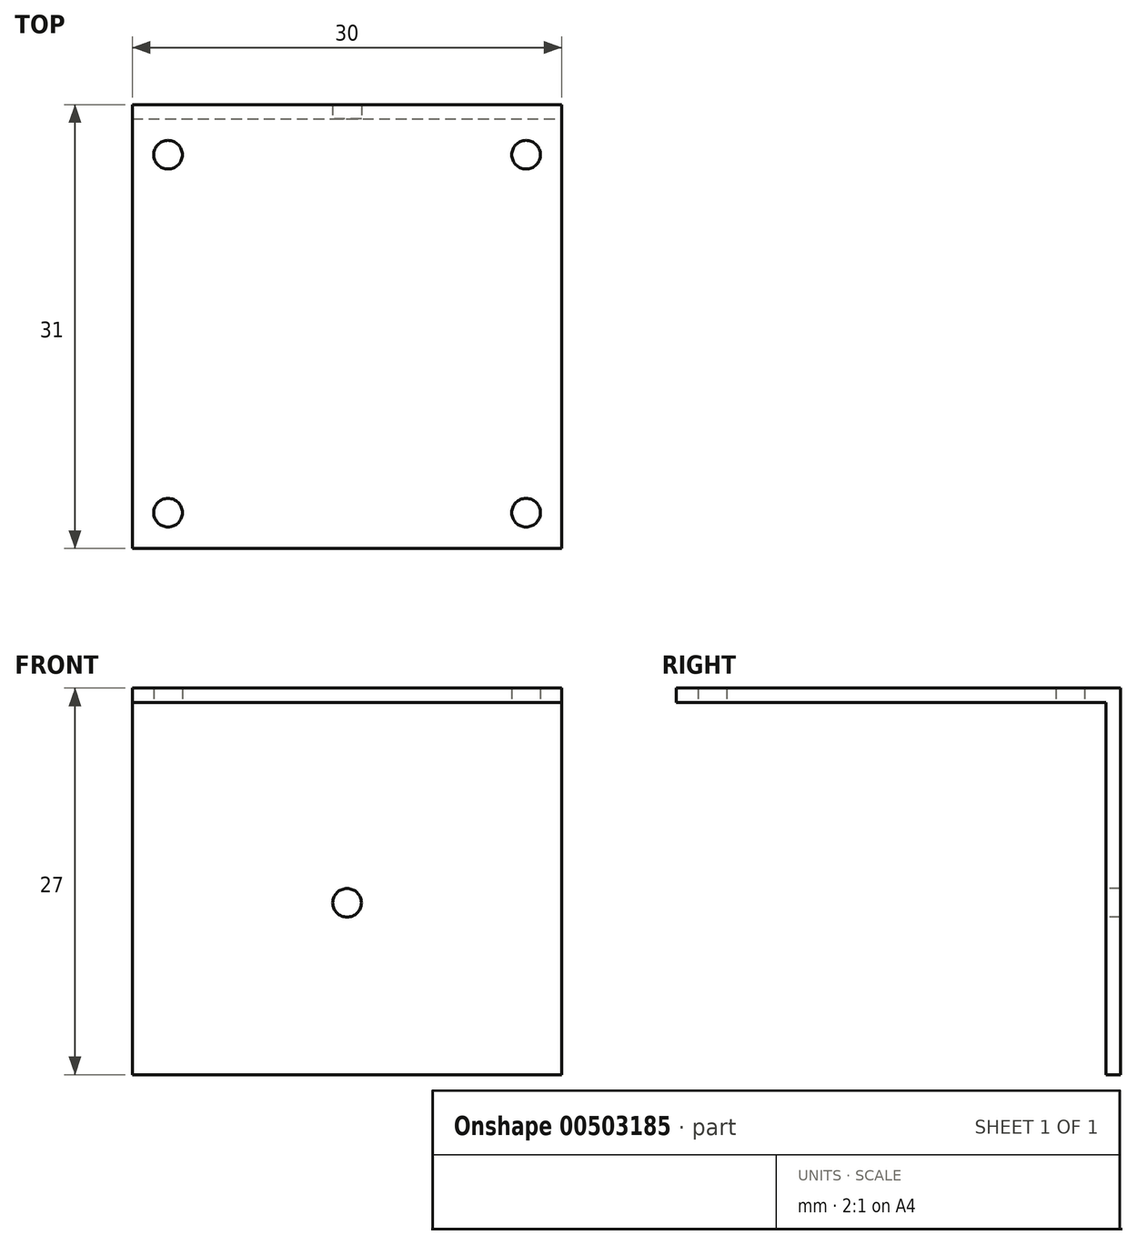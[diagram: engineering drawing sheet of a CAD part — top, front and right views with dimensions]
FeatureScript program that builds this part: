
annotation { "Feature Type Name" : "Feature", "Feature Type Description" : "" }
export const myFeature = defineFeature(function(context is Context, id is Id, definition is map)
    precondition{}
    {
        {
            var Q0;
            Q0=qCreatedBy(makeId("Top.planeOp"),FACE);
            var sketch = newSketch(context, id + "F0", { "sketchPlane" : qUnion([Q0])});
            skLineSegment(sketch, "E0.bottom", {"start": v(-15, 15) * mm, "end": v(15, 15) * mm});
            skLineSegment(sketch, "E0.top", {"start": v(-15, -15) * mm, "end": v(15, -15) * mm});
            skLineSegment(sketch, "E0.left", {"start": v(-15, 15) * mm, "end": v(-15, -15) * mm});
            skLineSegment(sketch, "E0.right", {"start": v(15, 15) * mm, "end": v(15, -15) * mm});
            skCircle(sketch, "E1", {"center": v(-12.5, -12.5) * mm, "radius": 1 * mm});
            skCircle(sketch, "E2.1.0.0", {"center": v(12.5, -12.5) * mm, "radius": 1 * mm});
            skCircle(sketch, "E3", {"center": v(-12.5, 12.5) * mm, "radius": 1 * mm});
            skCircle(sketch, "E4", {"center": v(12.5, 12.5) * mm, "radius": 1 * mm});
            skLineSegment(sketch, "E5.bottom", {"start": v(-12.5, 12.5) * mm, "end": v(12.5, 12.5) * mm, "construction": true});
            skLineSegment(sketch, "E5.top", {"start": v(-12.5, -12.5) * mm, "end": v(12.5, -12.5) * mm, "construction": true});
            skLineSegment(sketch, "E5.left", {"start": v(-12.5, 12.5) * mm, "end": v(-12.5, -12.5) * mm, "construction": true});
            skLineSegment(sketch, "E5.right", {"start": v(12.5, 12.5) * mm, "end": v(12.5, -12.5) * mm, "construction": true});
            skSolve(sketch);
        }
        {
            var Q0;
            Q0 = qSketchRegion(id + "F0", true);
            extrude(context, id + "F1", {"entities" : qUnion([Q0]), "depth" : 1 * mm});
        }
        {
            var Q0;
            Q0=makeQuery(id+"F1.opExtrude","SWEPT_FACE",FACE,{"disambiguationData":[OSD([sQuery(id+"F0.wireOp",EDGE,"E0.bottom")])]});
            var sketch = newSketch(context, id + "F2", { "sketchPlane" : qUnion([Q0])});
            skLineSegment(sketch, "E6.bottom", {"start": v(15, -26) * mm, "end": v(-15, -26) * mm});
            skLineSegment(sketch, "E6.top", {"start": v(15, 1) * mm, "end": v(-15, 1) * mm});
            skLineSegment(sketch, "E6.left", {"start": v(15, -26) * mm, "end": v(15, 1) * mm});
            skLineSegment(sketch, "E6.right", {"start": v(-15, -26) * mm, "end": v(-15, 1) * mm});
            skCircle(sketch, "E7", {"center": v(0, -14) * mm, "radius": 1 * mm});
            skSolve(sketch);
        }
        {
            var Q0;
            Q0 = qSketchRegion(id + "F2", true);
            extrude(context, id + "F3", {"entities" : qUnion([Q0]), "operationType" : NewBodyOperationType.ADD, "depth" : 1 * mm});
        }
    });
